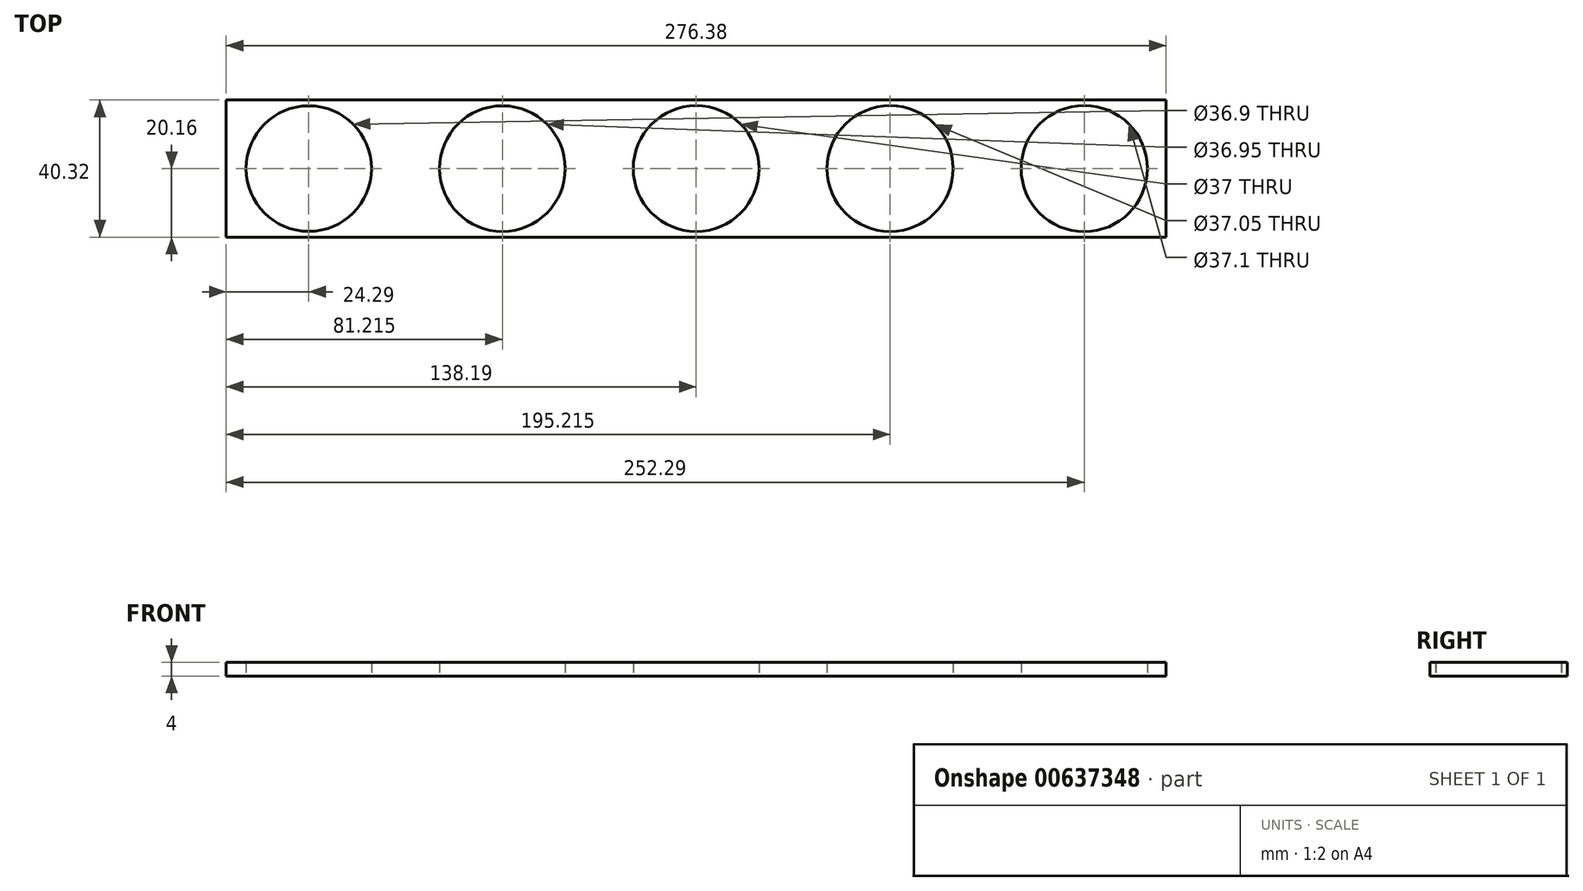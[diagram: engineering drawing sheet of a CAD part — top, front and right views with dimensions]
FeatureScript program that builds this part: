
annotation { "Feature Type Name" : "Feature", "Feature Type Description" : "" }
export const myFeature = defineFeature(function(context is Context, id is Id, definition is map)
    precondition{}
    {
        {
            var Q0;
            Q0=qCreatedBy(makeId("Top.planeOp"),FACE);
            var sketch = newSketch(context, id + "F0", { "sketchPlane" : qUnion([Q0])});
            skLineSegment(sketch, "E0", {"start": v(-80.84, 0) * mm, "end": v(86.24, 0) * mm, "construction": true});
            skCircle(sketch, "E1", {"center": v(-113.9, 0) * mm, "radius": 18.45 * mm});
            skCircle(sketch, "E2", {"center": v(-56.97, 0) * mm, "radius": 18.48 * mm});
            skCircle(sketch, "E3", {"center": v(0, 0) * mm, "radius": 18.5 * mm});
            skCircle(sketch, "E4", {"center": v(57.02, 0) * mm, "radius": 18.52 * mm});
            skCircle(sketch, "E5", {"center": v(114.1, 0) * mm, "radius": 18.55 * mm});
            skLineSegment(sketch, "E6.bottom", {"start": v(138.2, -20.16) * mm, "end": v(-138.2, -20.16) * mm});
            skLineSegment(sketch, "E6.top", {"start": v(138.2, 20.16) * mm, "end": v(-138.2, 20.16) * mm});
            skLineSegment(sketch, "E6.left", {"start": v(138.2, -20.16) * mm, "end": v(138.2, 20.16) * mm});
            skLineSegment(sketch, "E6.right", {"start": v(-138.2, -20.16) * mm, "end": v(-138.2, 20.16) * mm});
            skSolve(sketch);
        }
        {
            var Q0;
            Q0 = qSketchRegion(id + "F0", true);
            extrude(context, id + "F1", {"entities" : qUnion([Q0]), "depth" : 4 * mm, "offsetDistance" : 25 * mm});
        }
    });
